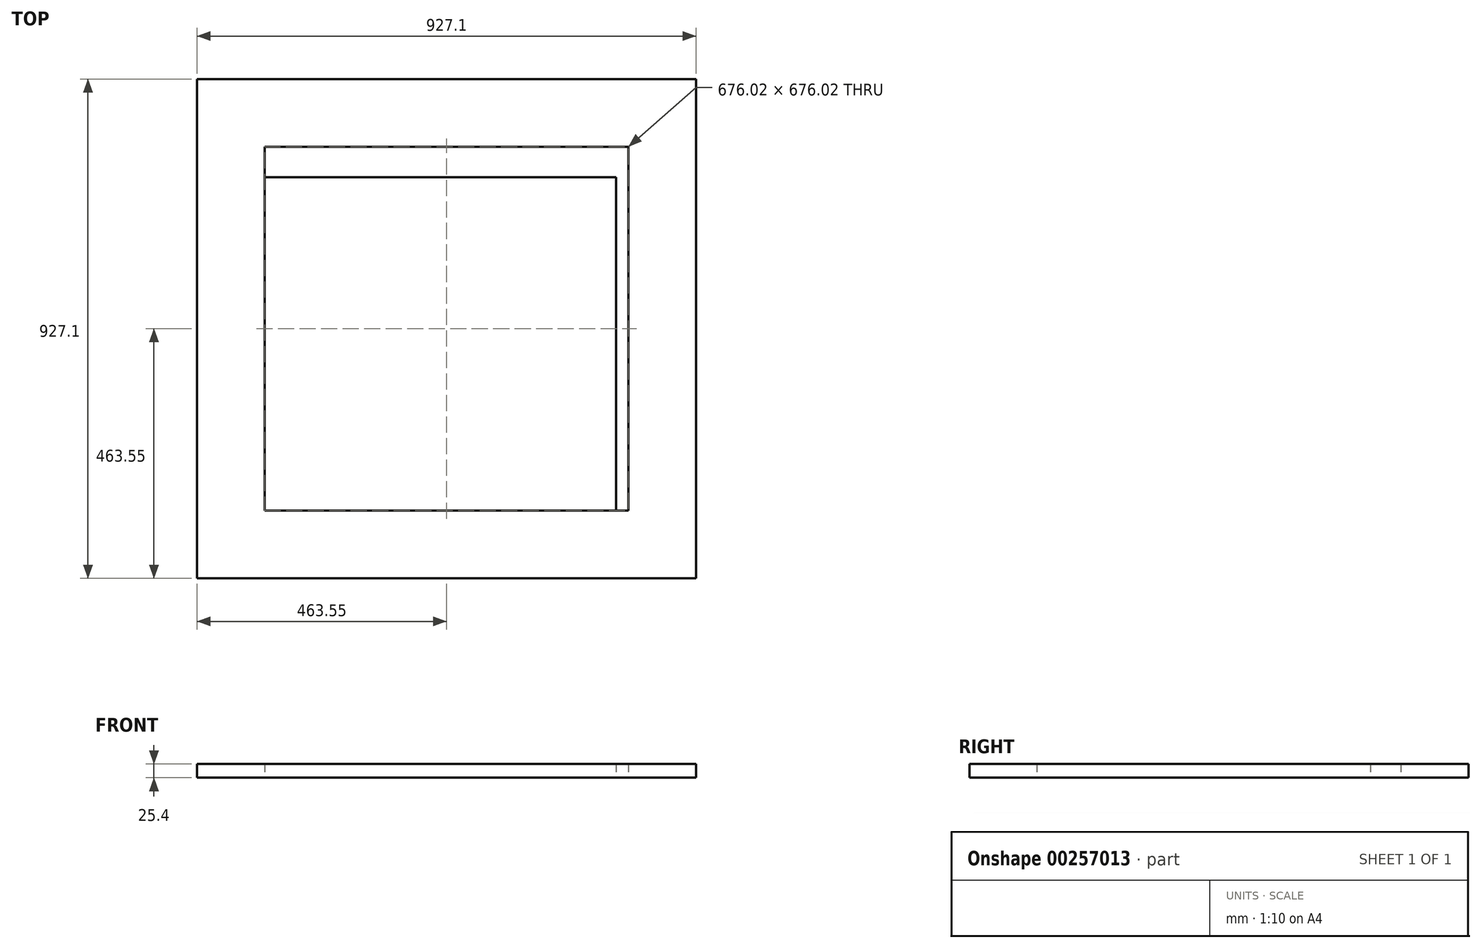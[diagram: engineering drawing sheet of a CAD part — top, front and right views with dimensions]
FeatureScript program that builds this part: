
annotation { "Feature Type Name" : "Feature", "Feature Type Description" : "" }
export const myFeature = defineFeature(function(context is Context, id is Id, definition is map)
    precondition{}
    {
        {
            var Q0;
            Q0=qCreatedBy(makeId("Top.planeOp"),FACE);
            var sketch = newSketch(context, id + "F0", { "sketchPlane" : qUnion([Q0])});
            skLineSegment(sketch, "E0.bottom", {"start": v(463.55, -463.55) * mm, "end": v(-463.55, -463.55) * mm});
            skLineSegment(sketch, "E0.top", {"start": v(463.55, 463.55) * mm, "end": v(-463.55, 463.55) * mm});
            skLineSegment(sketch, "E0.left", {"start": v(463.55, -463.55) * mm, "end": v(463.55, 463.55) * mm});
            skLineSegment(sketch, "E0.right", {"start": v(-463.55, -463.55) * mm, "end": v(-463.55, 463.55) * mm});
            skPoint(sketch, "E0.middle", {"position": v(0, 0) * mm});
            skLineSegment(sketch, "E1.bottom", {"start": v(338.01, -338.01) * mm, "end": v(-338.01, -338.01) * mm});
            skLineSegment(sketch, "E1.top", {"start": v(338.01, 338.01) * mm, "end": v(-338.01, 338.01) * mm});
            skLineSegment(sketch, "E1.left", {"start": v(338.01, -338.01) * mm, "end": v(338.01, 338.01) * mm});
            skLineSegment(sketch, "E1.right", {"start": v(-338.01, -338.01) * mm, "end": v(-338.01, 338.01) * mm});
            skSolve(sketch);
        }
        {
            var Q0;
            Q0 = qSketchRegion(id + "F0", true);
            extrude(context, id + "F1", {"entities" : qUnion([Q0]), "depth" : 25.4 * mm});
        }
        {
            var Q0;
            Q0=qCreatedBy(makeId("Top.planeOp"),FACE);
            var sketch = newSketch(context, id + "F2", { "sketchPlane" : qUnion([Q0])});
            skLineSegment(sketch, "E2.bottom", {"start": v(314.9, -338.01) * mm, "end": v(-338.01, -338.01) * mm});
            skLineSegment(sketch, "E2.top", {"start": v(314.9, 281.5) * mm, "end": v(-338.01, 281.5) * mm});
            skLineSegment(sketch, "E2.left", {"start": v(314.9, -338.01) * mm, "end": v(314.9, 281.5) * mm});
            skLineSegment(sketch, "E2.right", {"start": v(-338.01, -338.01) * mm, "end": v(-338.01, 281.5) * mm});
            skPoint(sketch, "E2.middle", {"position": v(-11.56, -28.26) * mm});
            skSolve(sketch);
        }
        {
            var Q0;
            Q0=makeQuery(id+"F2.imprint","IMPRINT",FACE,{"disambiguationData":[TD([[makeQuery(id+"F2.imprint","IMPRINT",EDGE,{"derivedFrom":sQuery(id+"F2.wireOp",EDGE,"E2.bottom")}),-1.0]])]});
            extrude(context, id + "F3", {"entities" : qUnion([Q0]), "depth" : 25.4 * mm});
        }
    });
